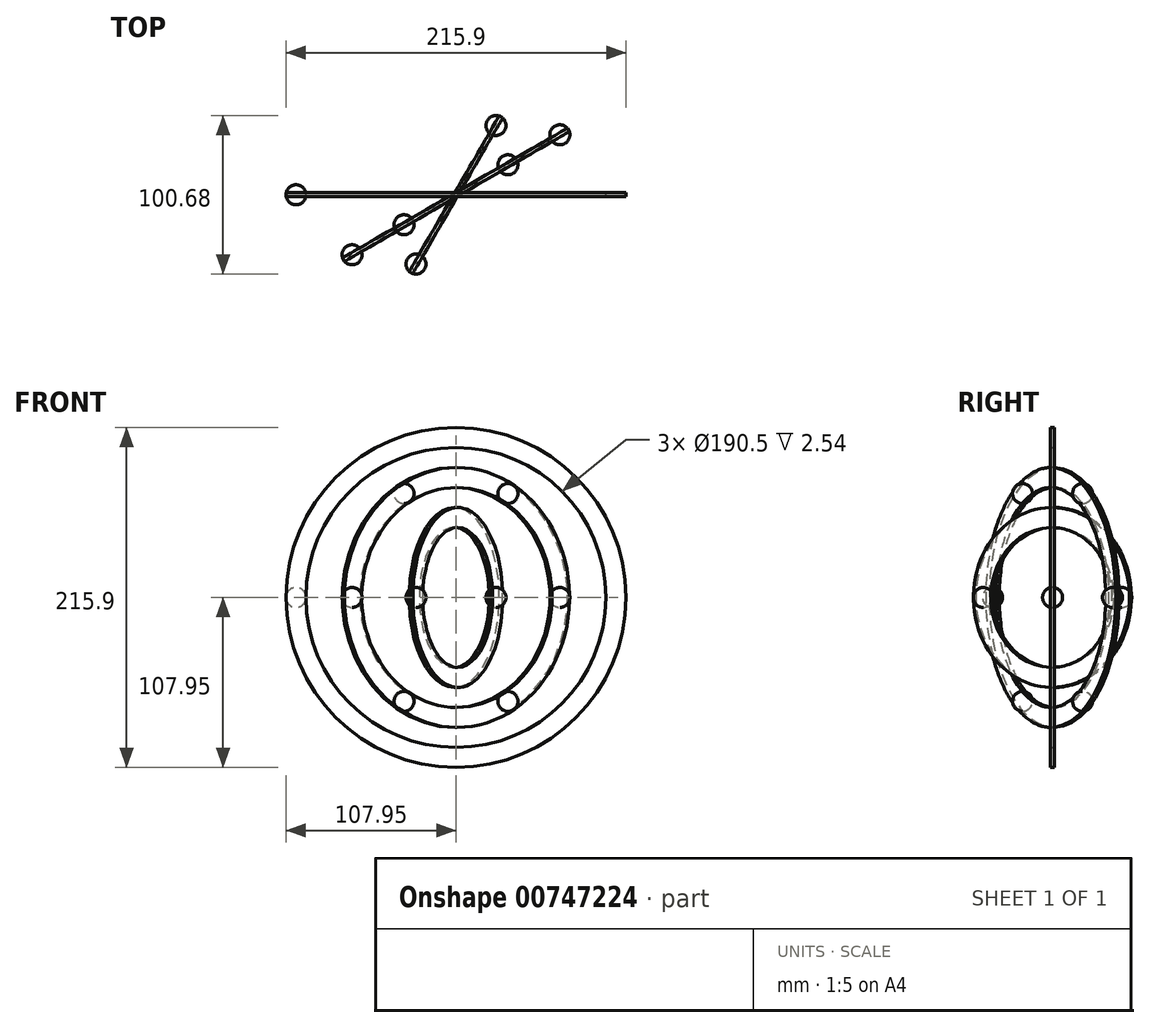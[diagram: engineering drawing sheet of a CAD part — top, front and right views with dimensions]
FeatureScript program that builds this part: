
annotation { "Feature Type Name" : "Feature", "Feature Type Description" : "" }
export const myFeature = defineFeature(function(context is Context, id is Id, definition is map)
    precondition{}
    {
        {
            var Q0;
            Q0=qCreatedBy(makeId("Front.planeOp"),FACE);
            var sketch = newSketch(context, id + "F0", { "sketchPlane" : qUnion([Q0])});
            skCircle(sketch, "E0", {"center": v(0, 0) * mm, "radius": 107.95 * mm});
            skCircle(sketch, "E1", {"center": v(0, 0) * mm, "radius": 95.25 * mm});
            skCircle(sketch, "E2", {"center": v(0, 0) * mm, "radius": 82.55 * mm});
            skCircle(sketch, "E3", {"center": v(0, 0) * mm, "radius": 69.85 * mm});
            skCircle(sketch, "E4", {"center": v(0, 0) * mm, "radius": 57.15 * mm});
            skCircle(sketch, "E5", {"center": v(0, 0) * mm, "radius": 44.45 * mm});
            skLineSegment(sketch, "E6", {"start": v(0, 0) * mm, "end": v(0, 26.62) * mm});
            skSolve(sketch);
        }
        {
            var Q0;
            Q0=makeQuery(id+"F0.imprint","IMPRINT",FACE,{"disambiguationData":[TD([[makeQuery(id+"F0.imprint","IMPRINT",EDGE,{"derivedFrom":sQuery(id+"F0.wireOp",EDGE,"E0")}),1.0]])]});
            extrude(context, id + "F1", {"entities" : qUnion([Q0]), "endBound" : BoundingType.SYMMETRIC, "depth" : 2.54 * mm, "offsetDistance" : 25.4 * mm});
        }
        {
            var Q0;
            Q0=makeQuery(id+"F0.imprint","IMPRINT",FACE,{"disambiguationData":[TD([[makeQuery(id+"F0.imprint","IMPRINT",EDGE,{"derivedFrom":sQuery(id+"F0.wireOp",EDGE,"E2")}),1.0]])]});
            extrude(context, id + "F2", {"entities" : qUnion([Q0]), "endBound" : BoundingType.SYMMETRIC, "oppositeDirection" : true, "depth" : 2.54 * mm, "offsetDistance" : 25.4 * mm});
        }
        {
            var Q0;
            Q0=makeQuery(id+"F0.imprint","IMPRINT",FACE,{"disambiguationData":[TD([[makeQuery(id+"F0.imprint","IMPRINT",EDGE,{"derivedFrom":sQuery(id+"F0.wireOp",EDGE,"E4")}),1.0]])]});
            extrude(context, id + "F3", {"entities" : qUnion([Q0]), "endBound" : BoundingType.SYMMETRIC, "depth" : 2.54 * mm, "offsetDistance" : 25.4 * mm});
        }
        {
            var Q0;
            Q0=makeQuery(id+"F2.opExtrude","SWEPT_BODY",BODY,{"disambiguationData":[OSD([sQuery(id+"F0.wireOp",EDGE,"E2"),sQuery(id+"F0.wireOp",EDGE,"E3")])]});
            var Q1;
            Q1=sQuery(id+"F0.wireOp",EDGE,"E6");
            transform(context, id + "F4", {"entities" : qUnion([Q0]), "transformType" : TransformType.ROTATION, "transformAxis" : qUnion([Q1]), "angle" : 30 * degree, "makeCopy" : false});
        }
        {
            var Q0;
            Q0=makeQuery(id+"F3.opExtrude","SWEPT_BODY",BODY,{"disambiguationData":[OSD([sQuery(id+"F0.wireOp",EDGE,"E4"),sQuery(id+"F0.wireOp",EDGE,"E5")])]});
            var Q1;
            Q1=sQuery(id+"F0.wireOp",EDGE,"E6");
            transform(context, id + "F5", {"entities" : qUnion([Q0]), "transformType" : TransformType.ROTATION, "transformAxis" : qUnion([Q1]), "angle" : 60 * degree, "makeCopy" : false});
        }
        {
            var Q0;
            Q0=makeQuery(id+"F3.opExtrude","CAP_FACE",FACE,{"disambiguationData":[OSD([sQuery(id+"F0.wireOp",EDGE,"E4"),sQuery(id+"F0.wireOp",EDGE,"E5")])],"isStart":false});
            cPlane(context, id + "F6", {"entities" : qUnion([Q0]), "cplaneType" : CPlaneType.OFFSET, "offset" : 1.27 * mm, "oppositeDirection" : true, "width" : 152.4 * mm, "height" : 152.4 * mm});
        }
        {
            var Q0;
            Q0=qCreatedBy(id+"F6.planeOp",FACE);
            var sketch = newSketch(context, id + "F7", { "sketchPlane" : qUnion([Q0])});
            skLineSegment(sketch, "E7", {"start": v(0, 0) * mm, "end": v(57.15, 0) * mm});
            skLineSegment(sketch, "E8", {"start": v(57.15, 0) * mm, "end": v(44.45, 0) * mm});
            skCircle(sketch, "E9", {"center": v(50.8, 0) * mm, "radius": 6.35 * mm});
            skLineSegment(sketch, "E10", {"start": v(0, 0) * mm, "end": v(-57.15, 0) * mm});
            skLineSegment(sketch, "E11", {"start": v(-57.15, 0) * mm, "end": v(-44.45, 0) * mm});
            skCircle(sketch, "E12", {"center": v(-50.8, 0) * mm, "radius": 6.35 * mm});
            skSolve(sketch);
        }
        {
            var Q0;
            {var subQ0=sQuery(id+"F7.wireOp",EDGE,"E12");var subQ1=sQuery(id+"F7.wireOp",EDGE,"E10");var subQ2=makeQuery(id+"F7.imprint","INTERSECT",VERTEX,{"disambiguationData":[OD(0.0)],"derivedFrom":[subQ1,subQ0]});Q0=makeQuery(id+"F7.imprint","IMPRINT",FACE,{"disambiguationData":[TD([[makeQuery(id+"F7.imprint","IMPRINT",EDGE,{"disambiguationData":[TD([[subQ2,1.0]])],"derivedFrom":subQ1}),-1.0]])]});}
            var Q1;
            {var subQ0=sQuery(id+"F7.wireOp",EDGE,"E9");var subQ1=sQuery(id+"F7.wireOp",EDGE,"E7");var subQ2=makeQuery(id+"F7.imprint","INTERSECT",VERTEX,{"disambiguationData":[OD(0.0)],"derivedFrom":[subQ1,subQ0]});Q1=makeQuery(id+"F7.imprint","IMPRINT",FACE,{"disambiguationData":[TD([[makeQuery(id+"F7.imprint","IMPRINT",EDGE,{"disambiguationData":[TD([[subQ2,1.0]])],"derivedFrom":subQ1}),1.0]])]});}
            var Q2;
            Q2=sQuery(id+"F7.wireOp",EDGE,"E10");
            revolve(context, id + "F8", {"surfaceOperationType" : NewSurfaceOperationType.NEW, "entities" : qUnion([Q0, Q1]), "axis" : qUnion([Q2]), "revolveType" : RevolveType.FULL});
        }
        {
            var Q0;
            Q0=makeQuery(id+"F2.opExtrude","CAP_FACE",FACE,{"disambiguationData":[OSD([sQuery(id+"F0.wireOp",EDGE,"E2"),sQuery(id+"F0.wireOp",EDGE,"E3")])],"isStart":true});
            cPlane(context, id + "F9", {"entities" : qUnion([Q0]), "cplaneType" : CPlaneType.OFFSET, "offset" : 1.27 * mm, "oppositeDirection" : true, "width" : 152.4 * mm, "height" : 152.4 * mm});
        }
        {
            var Q0;
            Q0=qCreatedBy(id+"F9.planeOp",FACE);
            var sketch = newSketch(context, id + "F10", { "sketchPlane" : qUnion([Q0])});
            skLineSegment(sketch, "E13", {"start": v(0, 0) * mm, "end": v(-82.55, 0) * mm});
            skLineSegment(sketch, "E14", {"start": v(-82.55, 0) * mm, "end": v(-69.85, 0) * mm});
            skCircle(sketch, "E15", {"center": v(-76.2, 0) * mm, "radius": 6.35 * mm});
            skCircle(sketch, "E16.1.0", {"center": v(-38.1, -66) * mm, "radius": 6.35 * mm});
            skLineSegment(sketch, "E16.1.1", {"start": v(-41.28, -71.5) * mm, "end": v(-34.93, -60.5) * mm});
            skCircle(sketch, "E16.2.0", {"center": v(38.1, -66) * mm, "radius": 6.35 * mm});
            skLineSegment(sketch, "E16.2.1", {"start": v(41.27, -71.5) * mm, "end": v(34.92, -60.5) * mm});
            skCircle(sketch, "E16.3.0", {"center": v(76.2, 0) * mm, "radius": 6.35 * mm});
            skLineSegment(sketch, "E16.3.1", {"start": v(82.55, 0) * mm, "end": v(69.85, 0) * mm});
            skCircle(sketch, "E16.4.0", {"center": v(38.1, 66) * mm, "radius": 6.35 * mm});
            skLineSegment(sketch, "E16.4.1", {"start": v(41.28, 71.5) * mm, "end": v(34.93, 60.5) * mm});
            skCircle(sketch, "E16.5.0", {"center": v(-38.1, 66) * mm, "radius": 6.35 * mm});
            skLineSegment(sketch, "E16.5.1", {"start": v(-41.28, 71.5) * mm, "end": v(-34.93, 60.5) * mm});
            skPoint(sketch, "E16.center", {"position": v(0, 0) * mm});
            skSolve(sketch);
        }
        {
            var Q0;
            {var subQ0=sQuery(id+"F10.wireOp",EDGE,"E15");var subQ1=sQuery(id+"F10.wireOp",EDGE,"E13");var subQ2=makeQuery(id+"F10.imprint","INTERSECT",VERTEX,{"disambiguationData":[OD(0.0)],"derivedFrom":[subQ1,subQ0]});Q0=makeQuery(id+"F10.imprint","IMPRINT",FACE,{"disambiguationData":[TD([[makeQuery(id+"F10.imprint","IMPRINT",EDGE,{"disambiguationData":[TD([[subQ2,1.0]])],"derivedFrom":subQ1}),-1.0]])]});}
            var Q1;
            {var subQ0=sQuery(id+"F10.wireOp",EDGE,"E16.3.1");Q1=makeQuery(id+"F10.imprint","IMPRINT",FACE,{"disambiguationData":[TD([[makeQuery(id+"F10.imprint","IMPRINT",EDGE,{"derivedFrom":subQ0}),-1.0]])]});}
            var Q2;
            Q2=sQuery(id+"F10.wireOp",EDGE,"E13");
            revolve(context, id + "F11", {"surfaceOperationType" : NewSurfaceOperationType.NEW, "entities" : qUnion([Q0, Q1]), "axis" : qUnion([Q2]), "revolveType" : RevolveType.FULL});
        }
        {
            var Q0;
            {var subQ0=sQuery(id+"F10.wireOp",EDGE,"E16.2.1");Q0=makeQuery(id+"F10.imprint","IMPRINT",FACE,{"disambiguationData":[TD([[makeQuery(id+"F10.imprint","IMPRINT",EDGE,{"derivedFrom":subQ0}),-1.0]])]});}
            var Q1;
            {var subQ0=sQuery(id+"F10.wireOp",EDGE,"E16.5.1");Q1=makeQuery(id+"F10.imprint","IMPRINT",FACE,{"disambiguationData":[TD([[makeQuery(id+"F10.imprint","IMPRINT",EDGE,{"derivedFrom":subQ0}),1.0]])]});}
            var Q2;
            Q2=sQuery(id+"F10.wireOp",EDGE,"E16.5.1");
            revolve(context, id + "F12", {"surfaceOperationType" : NewSurfaceOperationType.NEW, "entities" : qUnion([Q0, Q1]), "axis" : qUnion([Q2]), "revolveType" : RevolveType.FULL});
        }
        {
            var Q0;
            {var subQ0=sQuery(id+"F10.wireOp",EDGE,"E16.4.1");Q0=makeQuery(id+"F10.imprint","IMPRINT",FACE,{"disambiguationData":[TD([[makeQuery(id+"F10.imprint","IMPRINT",EDGE,{"derivedFrom":subQ0}),1.0]])]});}
            var Q1;
            {var subQ0=sQuery(id+"F10.wireOp",EDGE,"E16.1.1");Q1=makeQuery(id+"F10.imprint","IMPRINT",FACE,{"disambiguationData":[TD([[makeQuery(id+"F10.imprint","IMPRINT",EDGE,{"derivedFrom":subQ0}),-1.0]])]});}
            var Q2;
            Q2=sQuery(id+"F10.wireOp",EDGE,"E16.4.1");
            revolve(context, id + "F13", {"surfaceOperationType" : NewSurfaceOperationType.NEW, "entities" : qUnion([Q0, Q1]), "axis" : qUnion([Q2]), "revolveType" : RevolveType.FULL});
        }
        {
            var Q0;
            Q0=qCreatedBy(makeId("Front.planeOp"),FACE);
            var sketch = newSketch(context, id + "F14", { "sketchPlane" : qUnion([Q0])});
            skLineSegment(sketch, "E17", {"start": v(0, 0) * mm, "end": v(-107.95, 0) * mm});
            skLineSegment(sketch, "E18", {"start": v(-107.95, 0) * mm, "end": v(-95.25, 0) * mm});
            skCircle(sketch, "E19", {"center": v(-101.6, 0) * mm, "radius": 6.35 * mm});
            skSolve(sketch);
        }
        {
            var Q0;
            {var subQ0=sQuery(id+"F14.wireOp",EDGE,"E19");var subQ1=sQuery(id+"F14.wireOp",EDGE,"E17");var subQ2=makeQuery(id+"F14.imprint","INTERSECT",VERTEX,{"disambiguationData":[OD(0.0)],"derivedFrom":[subQ1,subQ0]});Q0=makeQuery(id+"F14.imprint","IMPRINT",FACE,{"disambiguationData":[TD([[makeQuery(id+"F14.imprint","IMPRINT",EDGE,{"disambiguationData":[TD([[subQ2,1.0]])],"derivedFrom":subQ1}),-1.0]])]});}
            var Q1;
            Q1=sQuery(id+"F14.wireOp",EDGE,"E18");
            revolve(context, id + "F15", {"surfaceOperationType" : NewSurfaceOperationType.NEW, "entities" : qUnion([Q0]), "axis" : qUnion([Q1]), "revolveType" : RevolveType.FULL});
        }
    });
